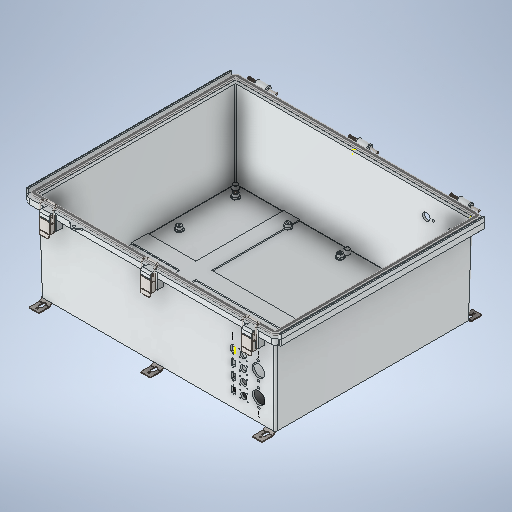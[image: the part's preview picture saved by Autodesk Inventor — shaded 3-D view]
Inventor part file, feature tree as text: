
AUTODESK INVENTOR PART (.ipt)
format: ipt  version: 2025 (Build 290162000, 162)  size: 6,532,096 bytes
history: native  units: mm
features: other x55, sketch x9, extrude x4, hole x1
ambient origin geometry x8: Origin, YZ Plane, XZ Plane, XY Plane, X Axis, Y Axis, Z Axis, Center Point
bodies: Solid1 (feature_tree), Solid2 (feature_tree), Solid3 (feature_tree), Solid4 (feature_tree), Solid5 (feature_tree), Solid6 (feature_tree), Solid7 (feature_tree), Solid8 (feature_tree), Solid9 (feature_tree), Solid10 (feature_tree), Solid11 (feature_tree), Solid12 (feature_tree), Solid13 (feature_tree), Solid14 (feature_tree), Solid15 (feature_tree), Solid16 (feature_tree), Solid17 (feature_tree), Solid18 (feature_tree), Solid19 (feature_tree), Solid20 (feature_tree), Solid21 (feature_tree), Solid22 (feature_tree), Solid23 (feature_tree), Solid24 (feature_tree), Solid25 (feature_tree), Solid26 (feature_tree), Solid27 (feature_tree), Solid28 (feature_tree), Solid29 (feature_tree), Solid30 (feature_tree), Solid31 (feature_tree), Solid32 (feature_tree), Solid33 (feature_tree), Solid34 (feature_tree), Solid35 (feature_tree), Solid36 (feature_tree), Solid37 (feature_tree), Solid38 (feature_tree), Solid39 (feature_tree), Solid40 (feature_tree), Solid41 (feature_tree), Solid42 (feature_tree), Solid43 (feature_tree), Solid44 (feature_tree), Solid45 (feature_tree), Solid46 (feature_tree), Solid47 (feature_tree), Solid48 (feature_tree), Solid49 (feature_tree), Solid50 (feature_tree), Solid51 (feature_tree), Solid52 (feature_tree), Solid53 (feature_tree), Solid54 (feature_tree)
feature tree (69):
  hole  "Coolant Ports"  [1 undecoded]
  extrude  "Fiberoptic Passthrough"  Depth=30.0mm
  extrude  "HV Mounts"  Depth=15.0mm
  extrude  "LV Mounts"  Depth=10.0mm
  other  "Port Labels"
  extrude  "Extrusion4"  Depth=10.0mm
  sketch  "Sketch8"  dims[d37=10.0mm d38=0.0mm d39=0.5mm d40=40.0mm d42=30.0mm d43=10.0mm d45=10.0mm d49=20.0mm d65=15.875mm d66=3.048mm d67=18.2626mm d68=18.2626mm d69=9.1313mm d70=9.1313mm d71=40.0mm d73=30.0mm d74=10.0mm d76=10.0mm d78=10.0mm d79=0.0mm d80=31.75mm d81=6.35mm d82=44.45mm d83=22.225mm d84=50.0mm d85=25.0mm d86=60.0mm d87=20.0mm d89=60.0mm d90=10.0mm d92=10.0mm d94=10.0mm d95=0.0mm d96=76.2mm d97=5.6mm d98=41.275mm d99=17.463mm d100=19.05mm d101=70.0mm d102=10.0mm d103=0.0mm d104=13.49375mm d105=25.0mm]
  sketch  "Sketch2"  dims[d11=50.0mm d12=50.0mm]
  sketch  "Sketch3"  dims[d15=12.7mm d16=6.0mm d17=4.0mm d18=2.0mm d19=90.0deg d20=8.0mm d21=20.594885mm d22=15.0mm]
  sketch  "Sketch Rectangular Pattern2"  dims[d13=30.0mm d14=30.0mm]
  sketch  "Sketch4"  dims[d23=10.0mm d24=20.0mm]
  sketch  "Sketch Rectangular Pattern4"  dims[d25=10.0mm d26=2.4mm]
  sketch  "Sketch6"  dims[d35=30.0mm]
  sketch  "Sketch Rectangular Pattern5"  dims[d27=2.4mm]
  sketch  "Sketch7"  dims[d36=100.0mm]
  other  "WQ-80B_WQ-80B-02_21:1"
  other  "WQ-80B_WQ-80B-02_21:2"
  other  "WQ-80B_WQ-80B-02_21:3"
  other  "WQ-80B_WQ-80B-02_21:4"
  other  "WQ-80B_WQ-80B-02_21:5"
  other  "WQ-80B_WQ-80B-02_21:6"
  other  "WQ-80B_WQ-80B-02_21:7"
  other  "WQ-80B_WQ-80B-02_21:8"
  other  "WQ-80B_WQ-80B-02_21:9"
  other  "WQ-80B_WQ-80B-02_21:10"
  other  "WQ-80B_WQ-80B-02_21:11"
  other  "WQ-80B_WQ-80B-02_21:12"
  other  "WQ-80B_WQ-80B-02_21:13"
  other  "WQ-80B_WQ-80B-02_21:14"
  other  "WQ-80B_WQ-80B-02_21:15"
  other  "WQ-80B_WQ-80B-02_21:16"
  other  "WQ-80B_WQ-80B-02_21:17"
  other  "WQ-80B_WQ-80B-02_21:18"
  other  "WQ-80B_WQ-80B-02_21:19"
  other  "WQ-80C_WQ-80C-02_22:1"
  other  "Door"
  other  "BASE^WQ-80L-01_29:1"
  other  "FRONT^WQ-80L-01_default_30:1"
  other  "PIN^WQ-80L-01_31:1"
  other  "LOOP^WQ-80L-01_32:1"
  other  "WQ-PIN-03_24:1"
  other  "BASE^WQ-80L-01_29:2"
  other  "FRONT^WQ-80L-01_default_30:2"
  other  "PIN^WQ-80L-01_31:2"
  other  "LOOP^WQ-80L-01_32:2"
  other  "BASE^WQ-80L-01_29:3"
  other  "FRONT^WQ-80L-01_default_30:3"
  other  "PIN^WQ-80L-01_31:3"
  other  "LOOP^WQ-80L-01_32:3"
  other  "WQ-PIN-03_27:1"
  other  "WQ-PIN-03_28:1"
  other  "WQ-92F_DEFAULT_3:1"
  other  "SCREWS-026_DEFAULT_4:1"
  other  "SCREWS-026_DEFAULT_5:1"
  other  "WQ-92F_DEFAULT_6:1"
  other  "SCREWS-026_DEFAULT_7:1"
  other  "SCREWS-026_DEFAULT_8:1"
  other  "WQ-92F_DEFAULT_9:1"
  other  "WQ-92F_DEFAULT_10:1"
  other  "SCREWS-026_DEFAULT_11:1"
  other  "SCREWS-026_DEFAULT_12:1"
  other  "SCREWS-026_DEFAULT_13:1"
  other  "SCREWS-026_DEFAULT_14:1"
  other  "WQ-92F_DEFAULT_15:1"
  other  "WQ-92F_DEFAULT_16:1"
  other  "SCREWS-026_DEFAULT_17:1"
  other  "SCREWS-026_DEFAULT_18:1"
  other  "SCREWS-026_DEFAULT_19:1"
  other  "SCREWS-026_DEFAULT_20:1"
note: 1 required parameter value undecoded (feature->parameter linkage not recoverable at this tier; creation-order binding heuristic only, values carry confidence <= 0.55)
